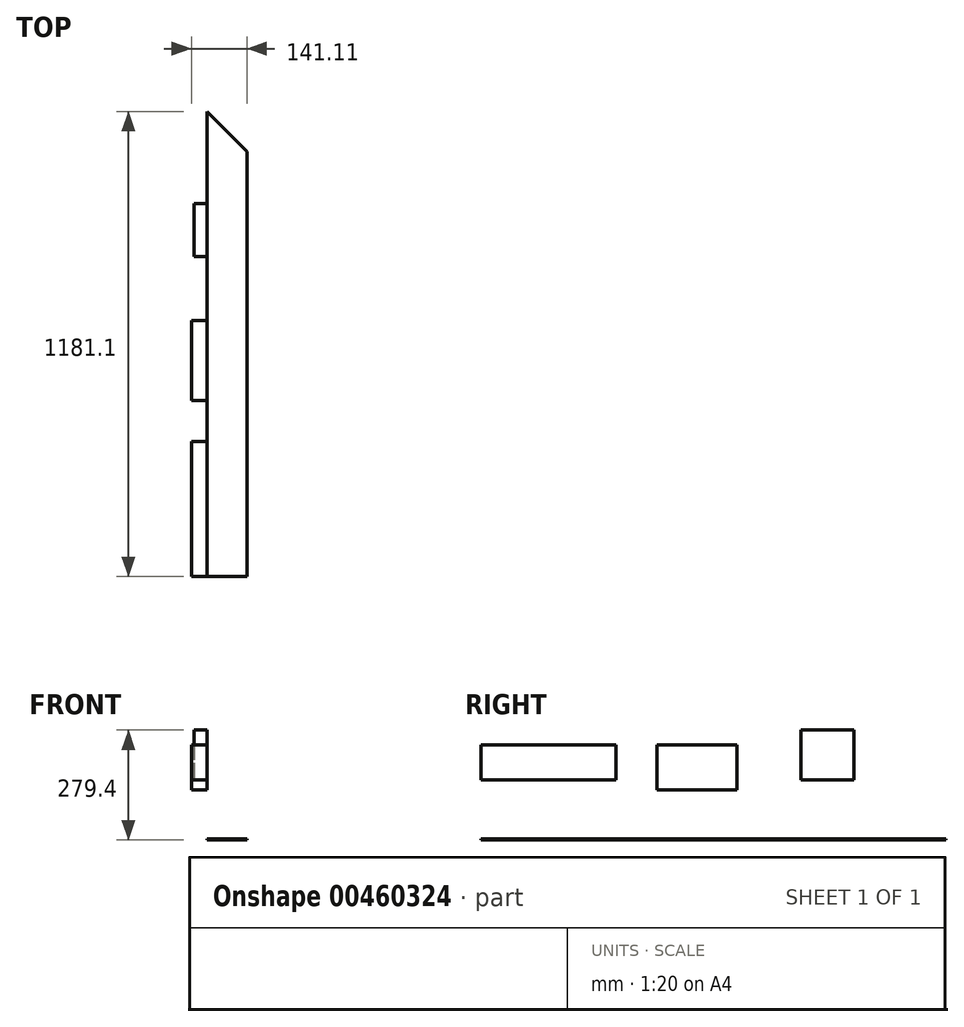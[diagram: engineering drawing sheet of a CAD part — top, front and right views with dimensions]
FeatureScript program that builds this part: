
annotation { "Feature Type Name" : "Feature", "Feature Type Description" : "" }
export const myFeature = defineFeature(function(context is Context, id is Id, definition is map)
    precondition{}
    {
        {
            var Q0;
            Q0=qCreatedBy(makeId("Top.planeOp"),FACE);
            var sketch = newSketch(context, id + "F0", { "sketchPlane" : qUnion([Q0])});
            skLineSegment(sketch, "E0", {"start": v(0, 1181.1) * mm, "end": v(0, 0) * mm});
            skLineSegment(sketch, "E1", {"start": v(0, 0) * mm, "end": v(101.6, 0) * mm});
            skLineSegment(sketch, "E2", {"start": v(101.6, 0) * mm, "end": v(101.6, 1079.5) * mm});
            skLineSegment(sketch, "E3", {"start": v(101.6, 1079.5) * mm, "end": v(0, 1181.1) * mm});
            skSolve(sketch);
        }
        {
            var Q0;
            Q0 = qSketchRegion(id + "F0", true);
            extrude(context, id + "F1", {"entities" : qUnion([Q0]), "depth" : 2.54 * mm});
        }
        {
            var Q0;
            Q0=qCreatedBy(makeId("Top.planeOp"),FACE);
            var sketch = newSketch(context, id + "F2", { "sketchPlane" : qUnion([Q0])});
            skLineSegment(sketch, "E4.bottom", {"start": v(0, 0) * mm, "end": v(-39.5, 0) * mm});
            skLineSegment(sketch, "E4.top", {"start": v(0, 342.9) * mm, "end": v(-39.5, 342.9) * mm});
            skLineSegment(sketch, "E4.left", {"start": v(0, 0) * mm, "end": v(0, 342.9) * mm});
            skLineSegment(sketch, "E4.right", {"start": v(-39.5, 0) * mm, "end": v(-39.5, 342.9) * mm});
            skLineSegment(sketch, "E5.bottom", {"start": v(0, 447.04) * mm, "end": v(-39.5, 447.04) * mm});
            skLineSegment(sketch, "E5.top", {"start": v(0, 650.24) * mm, "end": v(-39.5, 650.24) * mm});
            skLineSegment(sketch, "E5.left", {"start": v(0, 447.04) * mm, "end": v(0, 650.24) * mm});
            skLineSegment(sketch, "E5.right", {"start": v(-39.5, 447.04) * mm, "end": v(-39.5, 650.24) * mm});
            skLineSegment(sketch, "E6.bottom", {"start": v(0, 812.8) * mm, "end": v(-32.54, 812.8) * mm});
            skLineSegment(sketch, "E6.top", {"start": v(0, 947.42) * mm, "end": v(-32.54, 947.42) * mm});
            skLineSegment(sketch, "E6.left", {"start": v(0, 812.8) * mm, "end": v(0, 947.42) * mm});
            skLineSegment(sketch, "E6.right", {"start": v(-32.54, 812.8) * mm, "end": v(-32.54, 947.42) * mm});
            skSolve(sketch);
        }
        {
            var Q0;
            Q0=makeQuery(id+"F2.imprint","IMPRINT",FACE,{"disambiguationData":[TD([[makeQuery(id+"F2.imprint","IMPRINT",EDGE,{"derivedFrom":sQuery(id+"F2.wireOp",EDGE,"E4.bottom")}),-1.0]])]});
            extrude(context, id + "F3", {"entities" : qUnion([Q0]), "depth" : 241.3 * mm, "hasSecondDirection" : true, "secondDirectionOppositeDirection" : true, "secondDirectionDepth" : -152.4 * mm});
        }
        {
            var Q0;
            Q0=makeQuery(id+"F2.imprint","IMPRINT",FACE,{"disambiguationData":[TD([[makeQuery(id+"F2.imprint","IMPRINT",EDGE,{"derivedFrom":sQuery(id+"F2.wireOp",EDGE,"E5.bottom")}),-1.0]])]});
            extrude(context, id + "F4", {"entities" : qUnion([Q0]), "depth" : 241.3 * mm, "hasSecondDirection" : true, "secondDirectionOppositeDirection" : true, "secondDirectionDepth" : -127 * mm});
        }
        {
            var Q0;
            Q0=makeQuery(id+"F2.imprint","IMPRINT",FACE,{"disambiguationData":[TD([[makeQuery(id+"F2.imprint","IMPRINT",EDGE,{"derivedFrom":sQuery(id+"F2.wireOp",EDGE,"E6.bottom")}),-1.0]])]});
            extrude(context, id + "F5", {"entities" : qUnion([Q0]), "depth" : 279.4 * mm, "hasSecondDirection" : true, "secondDirectionOppositeDirection" : true, "secondDirectionDepth" : -152.4 * mm});
        }
    });
